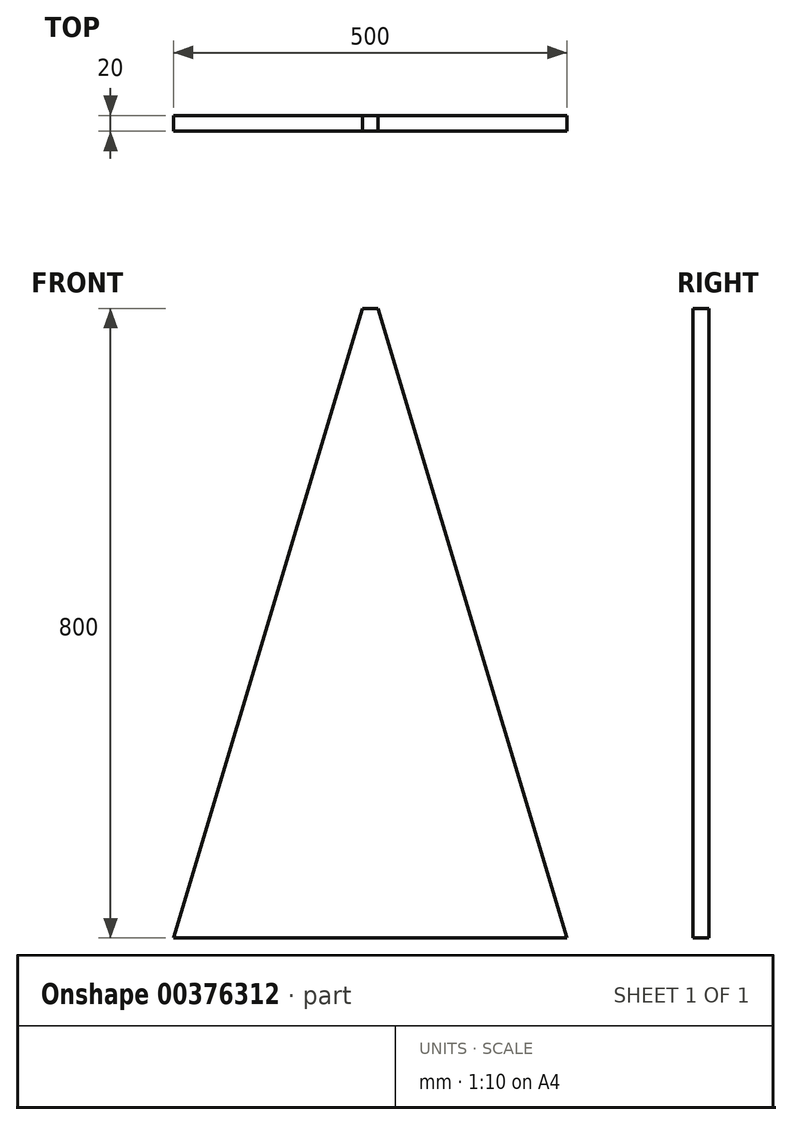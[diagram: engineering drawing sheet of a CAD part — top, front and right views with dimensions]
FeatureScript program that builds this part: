
annotation { "Feature Type Name" : "Feature", "Feature Type Description" : "" }
export const myFeature = defineFeature(function(context is Context, id is Id, definition is map)
    precondition{}
    {
        {
            assignVariable(context, id + "F0", {"name" : "BaseXLen", "anyValue" : 500 * mm});
        }
        {
            assignVariable(context, id + "F1", {"name" : "BaseZLen", "anyValue" : 800 * mm});
        }
        {
            var Q0;
            Q0=qCreatedBy(makeId("Front.planeOp"),FACE);
            var sketch = newSketch(context, id + "F2", { "sketchPlane" : qUnion([Q0])});
            skLineSegment(sketch, "E0.bottom", {"start": v(-250, 800) * mm, "end": v(250, 800) * mm});
            skLineSegment(sketch, "E0.top", {"start": v(-250, 0) * mm, "end": v(250, 0) * mm});
            skLineSegment(sketch, "E0.left", {"start": v(-250, 800) * mm, "end": v(-250, 0) * mm});
            skLineSegment(sketch, "E0.right", {"start": v(250, 800) * mm, "end": v(250, 0) * mm});
            skSolve(sketch);
        }
        {
            var Q0;
            Q0=makeQuery(id+"F2.imprint","IMPRINT",FACE,{"disambiguationData":[TD([[makeQuery(id+"F2.imprint","IMPRINT",EDGE,{"derivedFrom":sQuery(id+"F2.wireOp",EDGE,"E0.bottom")}),-1.0]])]});
            extrude(context, id + "F3", {"entities" : qUnion([Q0]), "depth" : 20 * mm});
        }
        {
            var Q0;
            Q0=makeQuery(id+"F3.opExtrude","SWEPT_EDGE",EDGE,{"disambiguationData":[OSD([sQuery(id+"F2.wireOp",EDGE,"E0.bottom"),sQuery(id+"F2.wireOp",EDGE,"E0.right")])]});
            var Q1;
            Q1=makeQuery(id+"F3.opExtrude","SWEPT_EDGE",EDGE,{"disambiguationData":[OSD([sQuery(id+"F2.wireOp",EDGE,"E0.bottom"),sQuery(id+"F2.wireOp",EDGE,"E0.left")])]});
            chamfer(context, id + "F4", {"entities" : qUnion([Q0, Q1]), "chamferType" : ChamferType.TWO_OFFSETS, "width1" : (getVariable(context, 'BaseXLen') - 20 * mm) / 2, "oppositeDirection" : false, "width2" : getVariable(context, 'BaseZLen'), "tangentPropagation" : true});
        }
    });
